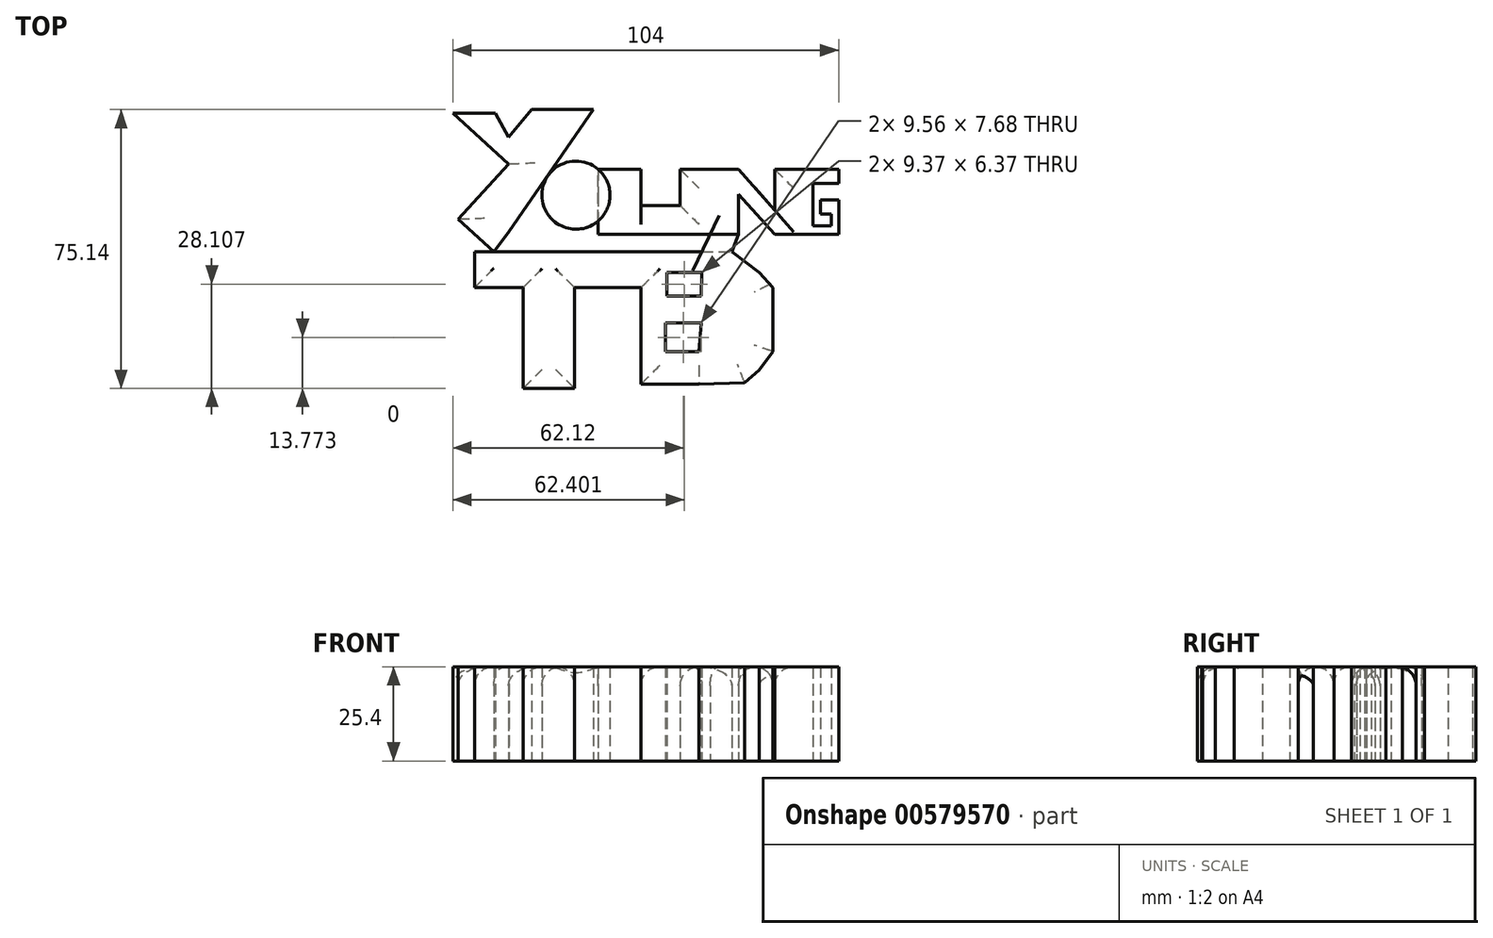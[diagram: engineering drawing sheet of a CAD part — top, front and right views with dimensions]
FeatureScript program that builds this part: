
annotation { "Feature Type Name" : "Feature", "Feature Type Description" : "" }
export const myFeature = defineFeature(function(context is Context, id is Id, definition is map)
    precondition{}
    {
        {
            var Q0;
            Q0=qCreatedBy(makeId("Top.planeOp"),FACE);
            var sketch = newSketch(context, id + "F0", { "sketchPlane" : qUnion([Q0])});
            skLineSegment(sketch, "E0", {"start": v(-35.5, 15.18) * mm, "end": v(-12.84, 47.97) * mm});
            skLineSegment(sketch, "E1", {"start": v(-12.84, 47.97) * mm, "end": v(-29.51, 47.97) * mm});
            skLineSegment(sketch, "E2", {"start": v(-29.51, 47.97) * mm, "end": v(-35.7, 40.47) * mm});
            skLineSegment(sketch, "E3", {"start": v(-35.7, 40.47) * mm, "end": v(-39.26, 47.03) * mm});
            skLineSegment(sketch, "E4", {"start": v(-39.26, 47.03) * mm, "end": v(-50.69, 47.03) * mm});
            skLineSegment(sketch, "E5", {"start": v(-50.69, 47.03) * mm, "end": v(-35.7, 33.35) * mm});
            skLineSegment(sketch, "E6", {"start": v(-35.7, 33.35) * mm, "end": v(-49.28, 18.47) * mm});
            skLineSegment(sketch, "E7", {"start": v(-49.28, 18.47) * mm, "end": v(-39.64, 9.66) * mm});
            skLineSegment(sketch, "E8", {"start": v(-39.64, 9.66) * mm, "end": v(-35.5, 15.18) * mm});
            skCircle(sketch, "E9", {"center": v(-17.52, 24.92) * mm, "radius": 9.18 * mm});
            skLineSegment(sketch, "E10", {"start": v(-5.9, 31.85) * mm, "end": v(-11.5, 31.85) * mm});
            skLineSegment(sketch, "E11", {"start": v(-11.5, 31.85) * mm, "end": v(0, 31.85) * mm});
            skLineSegment(sketch, "E12", {"start": v(0, 31.85) * mm, "end": v(0, 22.11) * mm});
            skLineSegment(sketch, "E13", {"start": v(0, 22.11) * mm, "end": v(10.59, 22.11) * mm});
            skLineSegment(sketch, "E14", {"start": v(10.59, 22.11) * mm, "end": v(10.59, 31.85) * mm});
            skLineSegment(sketch, "E15", {"start": v(10.59, 31.85) * mm, "end": v(18.64, 31.85) * mm});
            skLineSegment(sketch, "E16", {"start": v(18.64, 31.85) * mm, "end": v(18.64, 14.43) * mm});
            skLineSegment(sketch, "E17", {"start": v(18.64, 14.43) * mm, "end": v(-11.5, 14.43) * mm});
            skLineSegment(sketch, "E18", {"start": v(-11.5, 14.43) * mm, "end": v(-11.5, 31.85) * mm});
            skLineSegment(sketch, "E19", {"start": v(18.64, 31.85) * mm, "end": v(26.33, 31.85) * mm});
            skLineSegment(sketch, "E20", {"start": v(26.33, 31.85) * mm, "end": v(36.07, 20.8) * mm});
            skLineSegment(sketch, "E21", {"start": v(36.07, 20.8) * mm, "end": v(36.07, 31.85) * mm});
            skLineSegment(sketch, "E22", {"start": v(36.07, 31.85) * mm, "end": v(43.75, 31.85) * mm});
            skLineSegment(sketch, "E23", {"start": v(43.75, 31.85) * mm, "end": v(43.75, 14.43) * mm});
            skLineSegment(sketch, "E24", {"start": v(43.75, 14.43) * mm, "end": v(36.07, 14.43) * mm});
            skLineSegment(sketch, "E25", {"start": v(36.07, 14.43) * mm, "end": v(26.33, 25.1) * mm});
            skLineSegment(sketch, "E26", {"start": v(26.33, 25.1) * mm, "end": v(26.33, 14.43) * mm});
            skLineSegment(sketch, "E27", {"start": v(26.33, 14.43) * mm, "end": v(18.64, 14.43) * mm});
            skLineSegment(sketch, "E28", {"start": v(53.3, 31.85) * mm, "end": v(43.75, 31.85) * mm});
            skLineSegment(sketch, "E29", {"start": v(43.75, 14.43) * mm, "end": v(53.3, 14.43) * mm});
            skLineSegment(sketch, "E30", {"start": v(53.3, 14.43) * mm, "end": v(53.3, 23.6) * mm});
            skLineSegment(sketch, "E31", {"start": v(53.3, 23.6) * mm, "end": v(48.44, 23.6) * mm});
            skLineSegment(sketch, "E32", {"start": v(48.44, 23.6) * mm, "end": v(48.44, 19.77) * mm});
            skPoint(sketch, "E32.endSnap0", {"position": v(31.2, 19.77) * mm});
            skLineSegment(sketch, "E33", {"start": v(48.44, 19.77) * mm, "end": v(51.25, 19.77) * mm});
            skLineSegment(sketch, "E34", {"start": v(51.25, 19.77) * mm, "end": v(51.25, 16.68) * mm});
            skLineSegment(sketch, "E35", {"start": v(51.25, 16.68) * mm, "end": v(46.38, 16.68) * mm});
            skLineSegment(sketch, "E36", {"start": v(46.38, 16.68) * mm, "end": v(46.38, 28.1) * mm});
            skLineSegment(sketch, "E37", {"start": v(46.38, 28.1) * mm, "end": v(53.3, 28.1) * mm});
            skLineSegment(sketch, "E38", {"start": v(53.3, 28.1) * mm, "end": v(53.3, 31.85) * mm});
            skLineSegment(sketch, "E39", {"start": v(-39.64, 9.66) * mm, "end": v(0, 9.66) * mm});
            skLineSegment(sketch, "E40", {"start": v(0, 9.66) * mm, "end": v(0, 0) * mm});
            skLineSegment(sketch, "E41", {"start": v(0, 0) * mm, "end": v(-17.9, 0) * mm});
            skLineSegment(sketch, "E42", {"start": v(-17.9, 0) * mm, "end": v(-17.9, -27.17) * mm});
            skLineSegment(sketch, "E43", {"start": v(-17.9, -27.17) * mm, "end": v(-31.76, -27.17) * mm});
            skLineSegment(sketch, "E44", {"start": v(-31.76, -27.17) * mm, "end": v(-31.76, 0) * mm});
            skLineSegment(sketch, "E45", {"start": v(-31.76, 0) * mm, "end": v(-44.88, 0) * mm});
            skLineSegment(sketch, "E46", {"start": v(-44.88, 0) * mm, "end": v(-44.88, 9.66) * mm});
            skLineSegment(sketch, "E47", {"start": v(-44.88, 9.66) * mm, "end": v(-39.64, 9.66) * mm});
            skLineSegment(sketch, "E48", {"start": v(0, 9.66) * mm, "end": v(0, -26.05) * mm});
            skLineSegment(sketch, "E49", {"start": v(0, -26.05) * mm, "end": v(15.65, -26.05) * mm});
            skLineSegment(sketch, "E50", {"start": v(15.65, -26.05) * mm, "end": v(15.65, -17.24) * mm});
            skLineSegment(sketch, "E51", {"start": v(15.65, -17.24) * mm, "end": v(6.65, -17.24) * mm});
            skLineSegment(sketch, "E52", {"start": v(6.65, -17.24) * mm, "end": v(6.65, -9.56) * mm});
            skLineSegment(sketch, "E53", {"start": v(6.65, -9.56) * mm, "end": v(16.2, -9.56) * mm});
            skLineSegment(sketch, "E54", {"start": v(16.2, -9.56) * mm, "end": v(16.2, -2.25) * mm});
            skLineSegment(sketch, "E55", {"start": v(16.2, -2.25) * mm, "end": v(7.03, -2.25) * mm});
            skLineSegment(sketch, "E56", {"start": v(7.03, -2.25) * mm, "end": v(7.03, 4.12) * mm});
            skLineSegment(sketch, "E57", {"start": v(7.03, 4.12) * mm, "end": v(16.4, 4.12) * mm});
            skLineSegment(sketch, "E58", {"start": v(16.4, 4.12) * mm, "end": v(16.4, 9.66) * mm});
            skLineSegment(sketch, "E59", {"start": v(16.4, 9.66) * mm, "end": v(0, 9.66) * mm});
            skLineSegment(sketch, "E60", {"start": v(16.4, 9.66) * mm, "end": v(24.45, 9.66) * mm});
            skLineSegment(sketch, "E61", {"start": v(24.45, 9.66) * mm, "end": v(27.47, 7.4) * mm});
            skLineSegment(sketch, "E62", {"start": v(27.47, 7.4) * mm, "end": v(31.85, 4.12) * mm});
            skLineSegment(sketch, "E63", {"start": v(31.85, 4.12) * mm, "end": v(35.61, 0) * mm});
            skLineSegment(sketch, "E64", {"start": v(35.61, 0) * mm, "end": v(35.61, -17.24) * mm});
            skLineSegment(sketch, "E65", {"start": v(35.61, -17.24) * mm, "end": v(33.64, -19.87) * mm});
            skLineSegment(sketch, "E66", {"start": v(33.64, -19.87) * mm, "end": v(31.85, -22.26) * mm});
            skLineSegment(sketch, "E67", {"start": v(31.85, -22.26) * mm, "end": v(27.98, -25.68) * mm});
            skLineSegment(sketch, "E68", {"start": v(27.98, -25.68) * mm, "end": v(15.65, -26.05) * mm});
            skLineSegment(sketch, "E69", {"start": v(16.4, 4.12) * mm, "end": v(16.2, -2.25) * mm});
            skLineSegment(sketch, "E70", {"start": v(15.65, -17.24) * mm, "end": v(16.2, -9.56) * mm});
            skLineSegment(sketch, "E71", {"start": v(16.4, 9.66) * mm, "end": v(18.64, 14.43) * mm});
            skLineSegment(sketch, "E72", {"start": v(24.45, 9.66) * mm, "end": v(26.33, 14.43) * mm});
            skSolve(sketch);
        }
        {
            var Q0;
            Q0=makeQuery(id+"F0.imprint","IMPRINT",FACE,{"disambiguationData":[TD([[makeQuery(id+"F0.imprint","IMPRINT",EDGE,{"derivedFrom":sQuery(id+"F0.wireOp",EDGE,"E0")}),1.0]])]});
            var Q1;
            {var subQ0=sQuery(id+"F0.wireOp",EDGE,"E18");var subQ1=sQuery(id+"F0.wireOp",EDGE,"E9");var subQ3=makeQuery(id+"F0.imprint","INTERSECT",VERTEX,{"derivedFrom":[subQ1,subQ0]});Q1=makeQuery(id+"F0.imprint","IMPRINT",FACE,{"disambiguationData":[TD([[makeQuery(id+"F0.imprint","IMPRINT",EDGE,{"disambiguationData":[TD([[subQ3,1.0]])],"derivedFrom":subQ1}),1.0]])]});}
            var Q2;
            {var subQ0=sQuery(id+"F0.wireOp",EDGE,"E12");Q2=makeQuery(id+"F0.imprint","IMPRINT",FACE,{"disambiguationData":[TD([[makeQuery(id+"F0.imprint","IMPRINT",EDGE,{"derivedFrom":subQ0}),-1.0]])]});}
            var Q3;
            Q3=makeQuery(id+"F0.imprint","IMPRINT",FACE,{"disambiguationData":[TD([[makeQuery(id+"F0.imprint","IMPRINT",EDGE,{"derivedFrom":sQuery(id+"F0.wireOp",EDGE,"E16")}),1.0]])]});
            var Q4;
            Q4=makeQuery(id+"F0.imprint","IMPRINT",FACE,{"disambiguationData":[TD([[makeQuery(id+"F0.imprint","IMPRINT",EDGE,{"derivedFrom":sQuery(id+"F0.wireOp",EDGE,"E23")}),1.0]])]});
            var Q5;
            {var subQ1=sQuery(id+"F0.wireOp",EDGE,"E39");Q5=makeQuery(id+"F0.imprint","IMPRINT",FACE,{"disambiguationData":[TD([[makeQuery(id+"F0.imprint","IMPRINT",EDGE,{"derivedFrom":subQ1}),-1.0]])]});}
            var Q6;
            {var subQ3=sQuery(id+"F0.wireOp",EDGE,"E49");Q6=makeQuery(id+"F0.imprint","IMPRINT",FACE,{"disambiguationData":[TD([[makeQuery(id+"F0.imprint","IMPRINT",EDGE,{"derivedFrom":subQ3}),1.0]])]});}
            var Q7;
            Q7=makeQuery(id+"F0.imprint","IMPRINT",FACE,{"disambiguationData":[TD([[makeQuery(id+"F0.imprint","IMPRINT",EDGE,{"derivedFrom":sQuery(id+"F0.wireOp",EDGE,"E50")}),-1.0]])]});
            extrude(context, id + "F1", {"entities" : qUnion([Q0, Q1, Q2, Q3, Q4, Q5, Q6, Q7]), "depth" : 25.4 * mm, "offsetDistance" : 25.4 * mm});
        }
        {
            var Q0;
            Q0 = qSketchRegion(id + "F0", true);
            extrude(context, id + "F2", {"entities" : qUnion([Q0]), "depth" : 25.4 * mm, "offsetDistance" : 25.4 * mm});
        }
        {
            var Q0;
            Q0=makeQuery(id+"F1.opExtrude","CAP_EDGE",EDGE,{"disambiguationData":[OSD([sQuery(id+"F0.wireOp",EDGE,"E43")])],"isStart":false});
            var Q1;
            Q1=makeQuery(id+"F1.opExtrude","CAP_EDGE",EDGE,{"disambiguationData":[OSD([sQuery(id+"F0.wireOp",EDGE,"E44")])],"isStart":false});
            var Q2;
            Q2=makeQuery(id+"F1.opExtrude","CAP_EDGE",EDGE,{"disambiguationData":[OSD([sQuery(id+"F0.wireOp",EDGE,"E45")])],"isStart":false});
            var Q3;
            Q3=makeQuery(id+"F1.opExtrude","CAP_EDGE",EDGE,{"disambiguationData":[OSD([sQuery(id+"F0.wireOp",EDGE,"E7")])],"isStart":false});
            var Q4;
            Q4=makeQuery(id+"F1.opExtrude","CAP_EDGE",EDGE,{"disambiguationData":[OSD([sQuery(id+"F0.wireOp",EDGE,"E6")])],"isStart":false});
            var Q5;
            Q5=makeQuery(id+"F1.opExtrude","CAP_EDGE",EDGE,{"disambiguationData":[OSD([sQuery(id+"F0.wireOp",EDGE,"E5")])],"isStart":false});
            var Q6;
            Q6=makeQuery(id+"F1.opExtrude","CAP_EDGE",EDGE,{"disambiguationData":[OSD([sQuery(id+"F0.wireOp",EDGE,"E46")])],"isStart":false});
            var Q7;
            Q7=makeQuery(id+"F1.opExtrude","CAP_EDGE",EDGE,{"disambiguationData":[OSD([sQuery(id+"F0.wireOp",EDGE,"E49")])],"isStart":false});
            var Q8;
            Q8=makeQuery(id+"F1.opExtrude","CAP_EDGE",EDGE,{"disambiguationData":[OSD([sQuery(id+"F0.wireOp",EDGE,"E42")])],"isStart":false});
            var Q9;
            Q9=makeQuery(id+"F1.opExtrude","CAP_EDGE",EDGE,{"disambiguationData":[OSD([sQuery(id+"F0.wireOp",EDGE,"E41")])],"isStart":false});
            var Q10;
            Q10=makeQuery(id+"F1.opExtrude","CAP_EDGE",EDGE,{"disambiguationData":[OSD([sQuery(id+"F0.wireOp",EDGE,"E48")])],"isStart":false});
            var Q11;
            Q11=makeQuery(id+"F1.opExtrude","CAP_EDGE",EDGE,{"disambiguationData":[OSD([sQuery(id+"F0.wireOp",EDGE,"E67")])],"isStart":false});
            var Q12;
            Q12=makeQuery(id+"F1.opExtrude","CAP_EDGE",EDGE,{"disambiguationData":[OSD([sQuery(id+"F0.wireOp",EDGE,"E65"),sQuery(id+"F0.wireOp",EDGE,"E66")])],"isStart":false});
            var Q13;
            Q13=makeQuery(id+"F1.opExtrude","CAP_EDGE",EDGE,{"disambiguationData":[OSD([sQuery(id+"F0.wireOp",EDGE,"E64")])],"isStart":false});
            var Q14;
            Q14=makeQuery(id+"F1.opExtrude","CAP_EDGE",EDGE,{"disambiguationData":[OSD([sQuery(id+"F0.wireOp",EDGE,"E61"),sQuery(id+"F0.wireOp",EDGE,"E62")])],"isStart":false});
            var Q15;
            Q15=makeQuery(id+"F1.opExtrude","CAP_EDGE",EDGE,{"disambiguationData":[OSD([sQuery(id+"F0.wireOp",EDGE,"E24"),sQuery(id+"F0.wireOp",EDGE,"E29")])],"isStart":false});
            var Q16;
            Q16=makeQuery(id+"F1.opExtrude","CAP_EDGE",EDGE,{"disambiguationData":[OSD([sQuery(id+"F0.wireOp",EDGE,"E30")])],"isStart":false});
            var Q17;
            Q17=makeQuery(id+"F1.opExtrude","CAP_EDGE",EDGE,{"disambiguationData":[OSD([sQuery(id+"F0.wireOp",EDGE,"E26")])],"isStart":false});
            fillet(context, id + "F3", {"entities" : qUnion([Q0, Q1, Q2, Q3, Q4, Q5, Q6, Q7, Q8, Q9, Q10, Q11, Q12, Q13, Q14, Q15, Q16, Q17]), "radius" : 5.08 * mm, "tangentPropagation" : true, "allowEdgeOverflow" : false});
        }
        {
            var Q0;
            Q0=makeQuery(id+"F1.opExtrude","CAP_EDGE",EDGE,{"disambiguationData":[OSD([sQuery(id+"F0.wireOp",EDGE,"E49")])],"isStart":false});
            var Q1;
            Q1=makeQuery(id+"F1.opExtrude","CAP_EDGE",EDGE,{"disambiguationData":[OSD([sQuery(id+"F0.wireOp",EDGE,"E42")])],"isStart":false});
            var Q2;
            Q2=makeQuery(id+"F1.opExtrude","SWEPT_EDGE",EDGE,{"disambiguationData":[OSD([sQuery(id+"F0.wireOp",EDGE,"E66"),sQuery(id+"F0.wireOp",EDGE,"E67")])]});
            var Q3;
            Q3=makeQuery(id+"F1.opExtrude","CAP_EDGE",EDGE,{"disambiguationData":[OSD([sQuery(id+"F0.wireOp",EDGE,"E65"),sQuery(id+"F0.wireOp",EDGE,"E66")])],"isStart":false});
            var Q4;
            Q4=makeQuery(id+"F1.opExtrude","CAP_EDGE",EDGE,{"disambiguationData":[OSD([sQuery(id+"F0.wireOp",EDGE,"E64")])],"isStart":false});
            var Q5;
            Q5=makeQuery(id+"F1.opExtrude","CAP_EDGE",EDGE,{"disambiguationData":[OSD([sQuery(id+"F0.wireOp",EDGE,"E61"),sQuery(id+"F0.wireOp",EDGE,"E62")])],"isStart":false});
            var Q6;
            Q6=makeQuery(id+"F2.opExtrude","CAP_EDGE",EDGE,{"disambiguationData":[OSD([sQuery(id+"F0.wireOp",EDGE,"E39"),sQuery(id+"F0.wireOp",EDGE,"E47"),sQuery(id+"F0.wireOp",EDGE,"E59")])],"isStart":false});
            var Q7;
            Q7=makeQuery(id+"F2.opExtrude","CAP_EDGE",EDGE,{"disambiguationData":[OSD([sQuery(id+"F0.wireOp",EDGE,"E17")])],"isStart":false});
            var Q8;
            {var subQ0=sQuery(id+"F0.wireOp",EDGE,"E18");var subQ1=sQuery(id+"F0.wireOp",EDGE,"E9");Q8=makeQuery(id+"F1.opExtrude","CAP_EDGE",EDGE,{"disambiguationData":[OSD([subQ1]),TDD([makeQuery(id+"F0.imprint","IMPRINT",EDGE,{"disambiguationData":[TD([[makeQuery(id+"F0.imprint","INTERSECT",VERTEX,{"derivedFrom":[subQ1,subQ0]}),1.0]])],"derivedFrom":subQ1})])],"isStart":false});}
            var Q9;
            Q9=makeQuery(id+"F1.opExtrude","CAP_EDGE",EDGE,{"disambiguationData":[OSD([sQuery(id+"F0.wireOp",EDGE,"E0")])],"isStart":false});
            var Q10;
            Q10=makeQuery(id+"F1.opExtrude","CAP_EDGE",EDGE,{"disambiguationData":[OSD([sQuery(id+"F0.wireOp",EDGE,"E6")])],"isStart":false});
            var Q11;
            Q11=makeQuery(id+"F1.opExtrude","CAP_EDGE",EDGE,{"disambiguationData":[OSD([sQuery(id+"F0.wireOp",EDGE,"E7")])],"isStart":false});
            var Q12;
            Q12=makeQuery(id+"F1.opExtrude","CAP_EDGE",EDGE,{"disambiguationData":[OSD([sQuery(id+"F0.wireOp",EDGE,"E44")])],"isStart":false});
            var Q13;
            Q13=makeQuery(id+"F1.opExtrude","CAP_EDGE",EDGE,{"disambiguationData":[OSD([sQuery(id+"F0.wireOp",EDGE,"E43")])],"isStart":false});
            var Q14;
            Q14=makeQuery(id+"F1.opExtrude","CAP_EDGE",EDGE,{"disambiguationData":[OSD([sQuery(id+"F0.wireOp",EDGE,"E46")])],"isStart":false});
            var Q15;
            Q15=makeQuery(id+"F1.opExtrude","CAP_EDGE",EDGE,{"disambiguationData":[OSD([sQuery(id+"F0.wireOp",EDGE,"E5")])],"isStart":false});
            var Q16;
            Q16=makeQuery(id+"F1.opExtrude","CAP_EDGE",EDGE,{"disambiguationData":[OSD([sQuery(id+"F0.wireOp",EDGE,"E4")])],"isStart":false});
            var Q17;
            Q17=makeQuery(id+"F1.opExtrude","CAP_EDGE",EDGE,{"disambiguationData":[OSD([sQuery(id+"F0.wireOp",EDGE,"E1")])],"isStart":false});
            var Q18;
            Q18=makeQuery(id+"F1.opExtrude","CAP_EDGE",EDGE,{"disambiguationData":[OSD([sQuery(id+"F0.wireOp",EDGE,"E2")])],"isStart":false});
            var Q19;
            Q19=makeQuery(id+"F1.opExtrude","CAP_EDGE",EDGE,{"disambiguationData":[OSD([sQuery(id+"F0.wireOp",EDGE,"E15"),sQuery(id+"F0.wireOp",EDGE,"E19")])],"isStart":false});
            var Q20;
            Q20=makeQuery(id+"F1.opExtrude","CAP_EDGE",EDGE,{"disambiguationData":[OSD([sQuery(id+"F0.wireOp",EDGE,"E14")])],"isStart":false});
            var Q21;
            Q21=makeQuery(id+"F1.opExtrude","CAP_EDGE",EDGE,{"disambiguationData":[OSD([sQuery(id+"F0.wireOp",EDGE,"E13")])],"isStart":false});
            var Q22;
            Q22=makeQuery(id+"F1.opExtrude","CAP_EDGE",EDGE,{"disambiguationData":[OSD([sQuery(id+"F0.wireOp",EDGE,"E21")])],"isStart":false});
            var Q23;
            Q23=makeQuery(id+"F1.opExtrude","CAP_EDGE",EDGE,{"disambiguationData":[OSD([sQuery(id+"F0.wireOp",EDGE,"E22"),sQuery(id+"F0.wireOp",EDGE,"E28")])],"isStart":false});
            fillet(context, id + "F4", {"entities" : qUnion([Q0, Q1, Q2, Q3, Q4, Q5, Q6, Q7, Q8, Q9, Q10, Q11, Q12, Q13, Q14, Q15, Q16, Q17, Q18, Q19, Q20, Q21, Q22, Q23]), "radius" : 5.08 * mm, "tangentPropagation" : true, "allowEdgeOverflow" : false});
        }
    });
